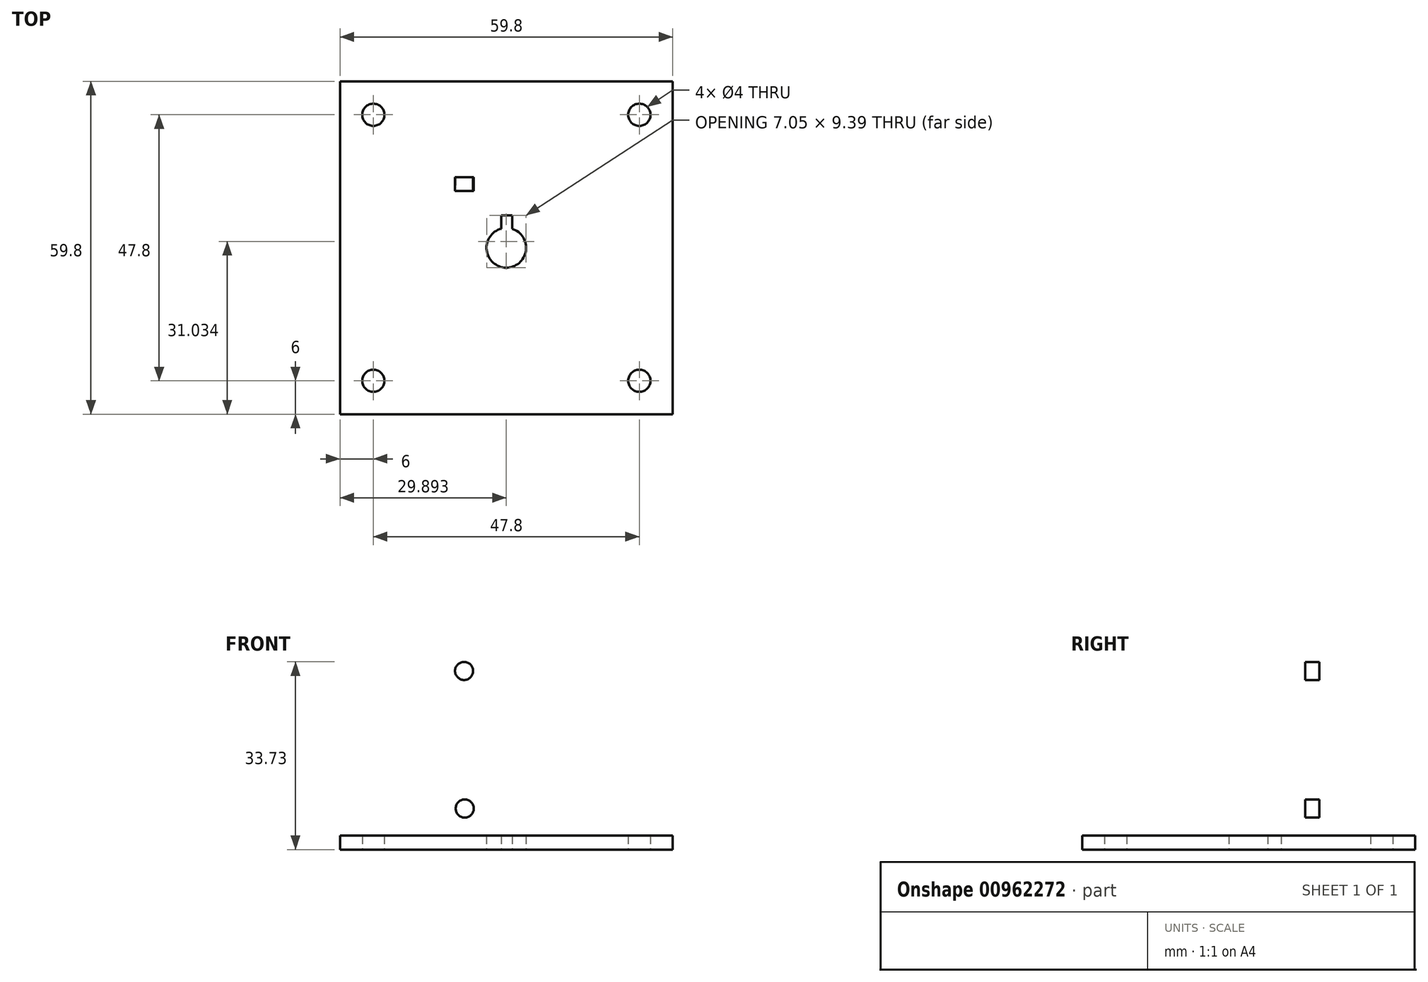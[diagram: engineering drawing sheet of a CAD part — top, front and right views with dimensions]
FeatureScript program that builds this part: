
annotation { "Feature Type Name" : "Feature", "Feature Type Description" : "" }
export const myFeature = defineFeature(function(context is Context, id is Id, definition is map)
    precondition{}
    {
        {
            var Q0;
            Q0=qCreatedBy(makeId("Top.planeOp"),FACE);
            var sketch = newSketch(context, id + "F0", { "sketchPlane" : qUnion([Q0])});
            skLineSegment(sketch, "E0.bottom", {"start": v(-29.9, 29.9) * mm, "end": v(29.9, 29.9) * mm});
            skLineSegment(sketch, "E0.top", {"start": v(-29.9, -29.9) * mm, "end": v(29.9, -29.9) * mm});
            skLineSegment(sketch, "E0.left", {"start": v(-29.9, 29.9) * mm, "end": v(-29.9, -29.9) * mm});
            skLineSegment(sketch, "E0.right", {"start": v(29.9, 29.9) * mm, "end": v(29.9, -29.9) * mm});
            skPoint(sketch, "E0.middle", {"position": v(0, 0) * mm});
            skCircle(sketch, "E1", {"center": v(0, 0) * mm, "radius": 3.56 * mm});
            skCircle(sketch, "E2", {"center": v(23.9, 23.9) * mm, "radius": 2 * mm});
            skLineSegment(sketch, "E3", {"start": v(0, 0) * mm, "end": v(0, 3.56) * mm, "construction": true});
            skLineSegment(sketch, "E4", {"start": v(0, 0) * mm, "end": v(-29.9, 0) * mm, "construction": true});
            skCircle(sketch, "E5.MirrorC", {"center": v(23.9, -23.9) * mm, "radius": 2 * mm});
            skLineSegment(sketch, "E6.MirrorCS", {"start": v(0, 0) * mm, "end": v(0, -29.9) * mm, "construction": true});
            skCircle(sketch, "E7.MirrorC", {"center": v(-23.9, 23.9) * mm, "radius": 2 * mm});
            skCircle(sketch, "E8.MirrorC", {"center": v(-23.9, -23.9) * mm, "radius": 2 * mm});
            skLineSegment(sketch, "E9", {"start": v(29.9, 10.2) * mm, "end": v(-10.1, 10.2) * mm});
            skLineSegment(sketch, "E10", {"start": v(-10.1, 10.2) * mm, "end": v(-10.1, 12.7) * mm});
            skLineSegment(sketch, "E11", {"start": v(-10.1, 12.7) * mm, "end": v(29.9, 12.7) * mm});
            skLineSegment(sketch, "E12.bottom", {"start": v(-0.93, 10.2) * mm, "end": v(0.9, 10.2) * mm});
            skLineSegment(sketch, "E13.trimOffspring", {"start": v(0, 5.17) * mm, "end": v(0, 29.9) * mm, "construction": true});
            skLineSegment(sketch, "E14.bottom", {"start": v(-0.93, 10.2) * mm, "end": v(1.03, 10.2) * mm});
            skLineSegment(sketch, "E14.top", {"start": v(-0.93, 3.4) * mm, "end": v(1.03, 3.4) * mm});
            skLineSegment(sketch, "E14.left", {"start": v(-0.93, 5.83) * mm, "end": v(-0.93, 3.4) * mm});
            skLineSegment(sketch, "E14.right", {"start": v(1.03, 5.83) * mm, "end": v(1.03, 3.4) * mm});
            skLineSegment(sketch, "E15", {"start": v(-0.93, 5.83) * mm, "end": v(1.03, 5.83) * mm});
            skSolve(sketch);
        }
        {
            var Q0;
            Q0=makeQuery(id+"F0.imprint","IMPRINT",FACE,{"disambiguationData":[TD([[makeQuery(id+"F0.imprint","IMPRINT",EDGE,{"derivedFrom":sQuery(id+"F0.wireOp",EDGE,"E0.bottom")}),-1.0]])]});
            extrude(context, id + "F1", {"entities" : qUnion([Q0]), "depth" : 2.5 * mm, "offsetDistance" : 25 * mm});
        }
        {
            var Q0;
            {var subQ0=sQuery(id+"F0.wireOp",EDGE,"E9");Q0=makeQuery(id+"F0.imprint","IMPRINT",FACE,{"disambiguationData":[TD([[makeQuery(id+"F0.imprint","IMPRINT",EDGE,{"derivedFrom":subQ0}),-1.0]])]});}
            extrude(context, id + "F2", {"entities" : qUnion([Q0]), "operationType" : NewBodyOperationType.ADD, "depth" : 40 * mm, "offsetDistance" : 25 * mm});
        }
        {
            var Q0;
            Q0=makeQuery(id+"F2.opExtrude","SWEPT_FACE",FACE,{"disambiguationData":[OSD([sQuery(id+"F0.wireOp",EDGE,"E9")])]});
            var sketch = newSketch(context, id + "F3", { "sketchPlane" : qUnion([Q0])});
            skCircle(sketch, "E16.MirrorC", {"center": v(-7.47, 7.38) * mm, "radius": 1.63 * mm});
            skCircle(sketch, "E17.MirrorC", {"center": v(-7.59, 32.1) * mm, "radius": 1.63 * mm});
            skLineSegment(sketch, "E18", {"start": v(9.9, 40) * mm, "end": v(9.9, 46.77) * mm, "construction": true});
            skCircle(sketch, "E19.MirrorC", {"center": v(27.39, 28.88) * mm, "radius": 1.63 * mm});
            skCircle(sketch, "E20.MirrorC", {"center": v(27.28, 7.38) * mm, "radius": 1.63 * mm});
            skSolve(sketch);
        }
        {
            var Q0;
            Q0=makeQuery(id+"F3.imprint","IMPRINT",FACE,{"disambiguationData":[TD([[makeQuery(id+"F3.imprint","IMPRINT",EDGE,{"derivedFrom":sQuery(id+"F3.wireOp",EDGE,"E17.MirrorC")}),-1.0]])]});
            var Q1;
            Q1=makeQuery(id+"F3.imprint","IMPRINT",FACE,{"disambiguationData":[TD([[makeQuery(id+"F3.imprint","IMPRINT",EDGE,{"derivedFrom":sQuery(id+"F3.wireOp",EDGE,"vH3Qvgiq-f8AB-glpA-LiBP-LjXX8R4j6ynJ")}),1.0]])]});
            var Q2;
            Q2=makeQuery(id+"F3.imprint","IMPRINT",FACE,{"disambiguationData":[TD([[makeQuery(id+"F3.imprint","IMPRINT",EDGE,{"derivedFrom":sQuery(id+"F3.wireOp",EDGE,"cxL52k3F-Gge5-dSNe-JZPn-7xtYMqMxKxmo")}),1.0]])]});
            var Q3;
            Q3=makeQuery(id+"F3.imprint","IMPRINT",FACE,{"disambiguationData":[TD([[makeQuery(id+"F3.imprint","IMPRINT",EDGE,{"derivedFrom":sQuery(id+"F3.wireOp",EDGE,"E16.MirrorC")}),-1.0]])]});
            var Q4;
            Q4=makeQuery(id+"F3.imprint","IMPRINT",FACE,{"disambiguationData":[TD([[makeQuery(id+"F3.imprint","IMPRINT",EDGE,{"derivedFrom":sQuery(id+"F3.wireOp",EDGE,"E19.MirrorC")}),1.0]])]});
            var Q5;
            Q5=makeQuery(id+"F3.imprint","IMPRINT",FACE,{"disambiguationData":[TD([[makeQuery(id+"F3.imprint","IMPRINT",EDGE,{"derivedFrom":sQuery(id+"F3.wireOp",EDGE,"E20.MirrorC")}),1.0]])]});
            extrude(context, id + "F4", {"entities" : qUnion([Q0, Q1, Q2, Q3, Q4, Q5]), "operationType" : NewBodyOperationType.REMOVE, "oppositeDirection" : true, "depth" : 25 * mm, "offsetDistance" : 25 * mm});
        }
    });
